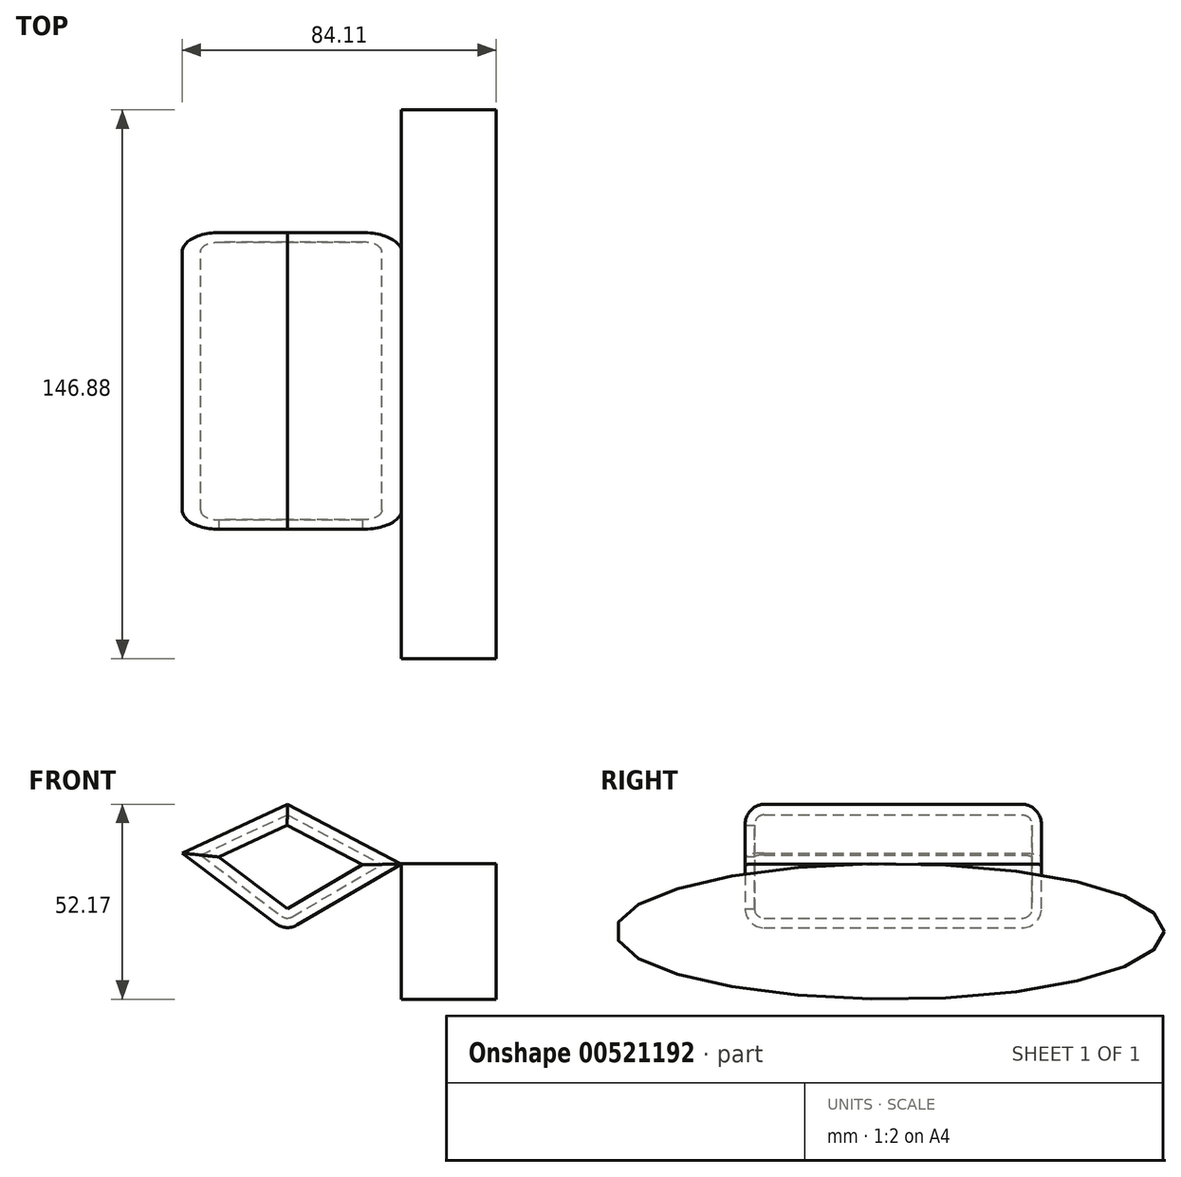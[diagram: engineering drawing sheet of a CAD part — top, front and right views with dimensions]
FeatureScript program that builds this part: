
annotation { "Feature Type Name" : "Feature", "Feature Type Description" : "" }
export const myFeature = defineFeature(function(context is Context, id is Id, definition is map)
    precondition{}
    {
        {
            var Q0;
            Q0=qCreatedBy(makeId("Right.planeOp"),FACE);
            var sketch = newSketch(context, id + "F0", { "sketchPlane" : qUnion([Q0])});
            skEllipse(sketch, "E0", {"center": v(0, 0) * mm, "majorRadius": 73.44 * mm, "minorRadius": 18.15 * mm, "majorAxis": v(1, 0)});
            skSolve(sketch);
        }
        {
            var Q0;
            Q0=makeQuery(id+"F0.imprint","IMPRINT",FACE,{"disambiguationData":[TD([[makeQuery(id+"F0.imprint","IMPRINT",EDGE,{"derivedFrom":sQuery(id+"F0.wireOp",EDGE,"E0")}),1.0]])]});
            extrude(context, id + "F1", {"entities" : qUnion([Q0]), "depth" : 25.4 * mm, "offsetDistance" : 25.4 * mm});
        }
        {
            var Q0;
            Q0=qCreatedBy(makeId("Front.planeOp"),FACE);
            var sketch = newSketch(context, id + "F2", { "sketchPlane" : qUnion([Q0])});
            skLineSegment(sketch, "E1", {"start": v(0, 18.05) * mm, "end": v(-19.3, 34.02) * mm});
            skLineSegment(sketch, "E2", {"start": v(-19.3, 34.02) * mm, "end": v(-41.7, 34.02) * mm});
            skLineSegment(sketch, "E3", {"start": v(-41.7, 34.02) * mm, "end": v(-58.71, 20.95) * mm});
            skLineSegment(sketch, "E4", {"start": v(-58.71, 20.95) * mm, "end": v(-30.5, 34.02) * mm});
            skLineSegment(sketch, "E5", {"start": v(-30.5, 34.02) * mm, "end": v(0, 18.05) * mm});
            skLineSegment(sketch, "E6", {"start": v(-58.71, 20.95) * mm, "end": v(-30.91, 0) * mm});
            skLineSegment(sketch, "E7", {"start": v(-30.91, 0) * mm, "end": v(0, 18.05) * mm});
            skSolve(sketch);
        }
        {
            var Q0;
            Q0=makeQuery(id+"F2.imprint","IMPRINT",FACE,{"disambiguationData":[TD([[makeQuery(id+"F2.imprint","IMPRINT",EDGE,{"derivedFrom":sQuery(id+"F2.wireOp",EDGE,"E4")}),-1.0]])]});
            extrude(context, id + "F3", {"entities" : qUnion([Q0]), "depth" : 25.4 * mm, "offsetDistance" : 25.4 * mm});
        }
        {
            var Q0;
            Q0=makeQuery(id+"F3.opExtrude","CAP_FACE",FACE,{"disambiguationData":[OSD([sQuery(id+"F2.wireOp",EDGE,"E4"),sQuery(id+"F2.wireOp",EDGE,"E5"),sQuery(id+"F2.wireOp",EDGE,"E6"),sQuery(id+"F2.wireOp",EDGE,"E7")])],"isStart":true});
            extrude(context, id + "F4", {"entities" : qUnion([Q0]), "operationType" : NewBodyOperationType.ADD, "depth" : 40.6 * mm, "offsetDistance" : 25.4 * mm});
        }
        {
            var Q0;
            Q0=makeQuery(id+"F3.opExtrude","CAP_FACE",FACE,{"disambiguationData":[OSD([sQuery(id+"F2.wireOp",EDGE,"E4"),sQuery(id+"F2.wireOp",EDGE,"E5"),sQuery(id+"F2.wireOp",EDGE,"E6"),sQuery(id+"F2.wireOp",EDGE,"E7")])],"isStart":false});
            extrude(context, id + "F5", {"entities" : qUnion([Q0]), "operationType" : NewBodyOperationType.ADD, "depth" : 13.44 * mm, "offsetDistance" : 25.4 * mm});
        }
        {
            var Q0;
            Q0=makeQuery(id+"F5.opExtrude","CAP_EDGE",EDGE,{"disambiguationData":[OSD([sQuery(id+"F2.wireOp",EDGE,"E5")])],"isStart":false});
            var Q1;
            Q1=makeQuery(id+"F5.opExtrude","CAP_EDGE",EDGE,{"disambiguationData":[OSD([sQuery(id+"F2.wireOp",EDGE,"E4")])],"isStart":false});
            var Q2;
            {var subQ0=sQuery(id+"F2.wireOp",EDGE,"E7");var subQ1=sQuery(id+"F2.wireOp",EDGE,"E6");Q2=makeQuery(id+"F5.boolean.opBoolean","MERGE",EDGE,{"derivedFrom":[makeQuery(id+"F4.boolean.opBoolean","MERGE",EDGE,{"derivedFrom":[makeQuery(id+"F3.opExtrude","SWEPT_EDGE",EDGE,{"disambiguationData":[OSD([subQ1,subQ0])]}),makeQuery(id+"F4.opExtrude","SWEPT_EDGE",EDGE,{"disambiguationData":[OSD([subQ1,subQ0])]})]}),makeQuery(id+"F5.opExtrude","SWEPT_EDGE",EDGE,{"disambiguationData":[OSD([subQ1,subQ0])]})]});}
            var Q3;
            Q3=makeQuery(id+"F5.opExtrude","CAP_EDGE",EDGE,{"disambiguationData":[OSD([sQuery(id+"F2.wireOp",EDGE,"E7")])],"isStart":false});
            var Q4;
            Q4=makeQuery(id+"F5.opExtrude","CAP_EDGE",EDGE,{"disambiguationData":[OSD([sQuery(id+"F2.wireOp",EDGE,"E6")])],"isStart":false});
            var Q5;
            Q5=makeQuery(id+"F4.opExtrude","CAP_EDGE",EDGE,{"disambiguationData":[OSD([sQuery(id+"F2.wireOp",EDGE,"E5")])],"isStart":false});
            var Q6;
            Q6=makeQuery(id+"F4.opExtrude","CAP_EDGE",EDGE,{"disambiguationData":[OSD([sQuery(id+"F2.wireOp",EDGE,"E4")])],"isStart":false});
            var Q7;
            Q7=makeQuery(id+"F4.opExtrude","CAP_EDGE",EDGE,{"disambiguationData":[OSD([sQuery(id+"F2.wireOp",EDGE,"E7")])],"isStart":false});
            var Q8;
            Q8=makeQuery(id+"F4.opExtrude","CAP_EDGE",EDGE,{"disambiguationData":[OSD([sQuery(id+"F2.wireOp",EDGE,"E6")])],"isStart":false});
            fillet(context, id + "F6", {"entities" : qUnion([Q0, Q1, Q2, Q3, Q4, Q5, Q6, Q7, Q8]), "radius" : 5.08 * mm, "tangentPropagation" : true, "allowEdgeOverflow" : false});
        }
        {
            var Q0;
            Q0=makeQuery(id+"F5.opExtrude","CAP_FACE",FACE,{"disambiguationData":[OSD([sQuery(id+"F2.wireOp",EDGE,"E4"),sQuery(id+"F2.wireOp",EDGE,"E5"),sQuery(id+"F2.wireOp",EDGE,"E6"),sQuery(id+"F2.wireOp",EDGE,"E7")])],"isStart":false});
            var sketch = newSketch(context, id + "F7", { "sketchPlane" : qUnion([Q0])});
            skLineSegment(sketch, "E8", {"start": v(-39.72, 13) * mm, "end": v(-20.52, 11.95) * mm});
            skLineSegment(sketch, "E9", {"start": v(-20.52, 11.95) * mm, "end": v(-30.55, 6.1) * mm});
            skLineSegment(sketch, "E10", {"start": v(-30.55, 6.1) * mm, "end": v(-39.72, 13) * mm});
            skSolve(sketch);
        }
        {
            var Q0;
            {var subQ8=sQuery(id+"F7.wireOp",EDGE,"E8");Q0=makeQuery(id+"F7.imprint","IMPRINT",FACE,{"disambiguationData":[TD([[makeQuery(id+"F7.imprint","IMPRINT",EDGE,{"derivedFrom":subQ8}),1.0]])]});}
            var Q1;
            Q1 = qSketchRegion(id + "F7", true);
            extrude(context, id + "F8", {"entities" : qUnion([Q0, Q1]), "operationType" : NewBodyOperationType.ADD, "oppositeDirection" : true, "depth" : 18 * mm, "offsetDistance" : 25.4 * mm});
        }
        {
            var Q0;
            Q0=makeQuery(id+"F5.opExtrude","CAP_FACE",FACE,{"disambiguationData":[OSD([sQuery(id+"F2.wireOp",EDGE,"E4"),sQuery(id+"F2.wireOp",EDGE,"E5"),sQuery(id+"F2.wireOp",EDGE,"E6"),sQuery(id+"F2.wireOp",EDGE,"E7")])],"isStart":false});
            shell(context, id + "F9", {"entities" : qUnion([Q0]), "thickness" : 2.54 * mm});
        }
    });
